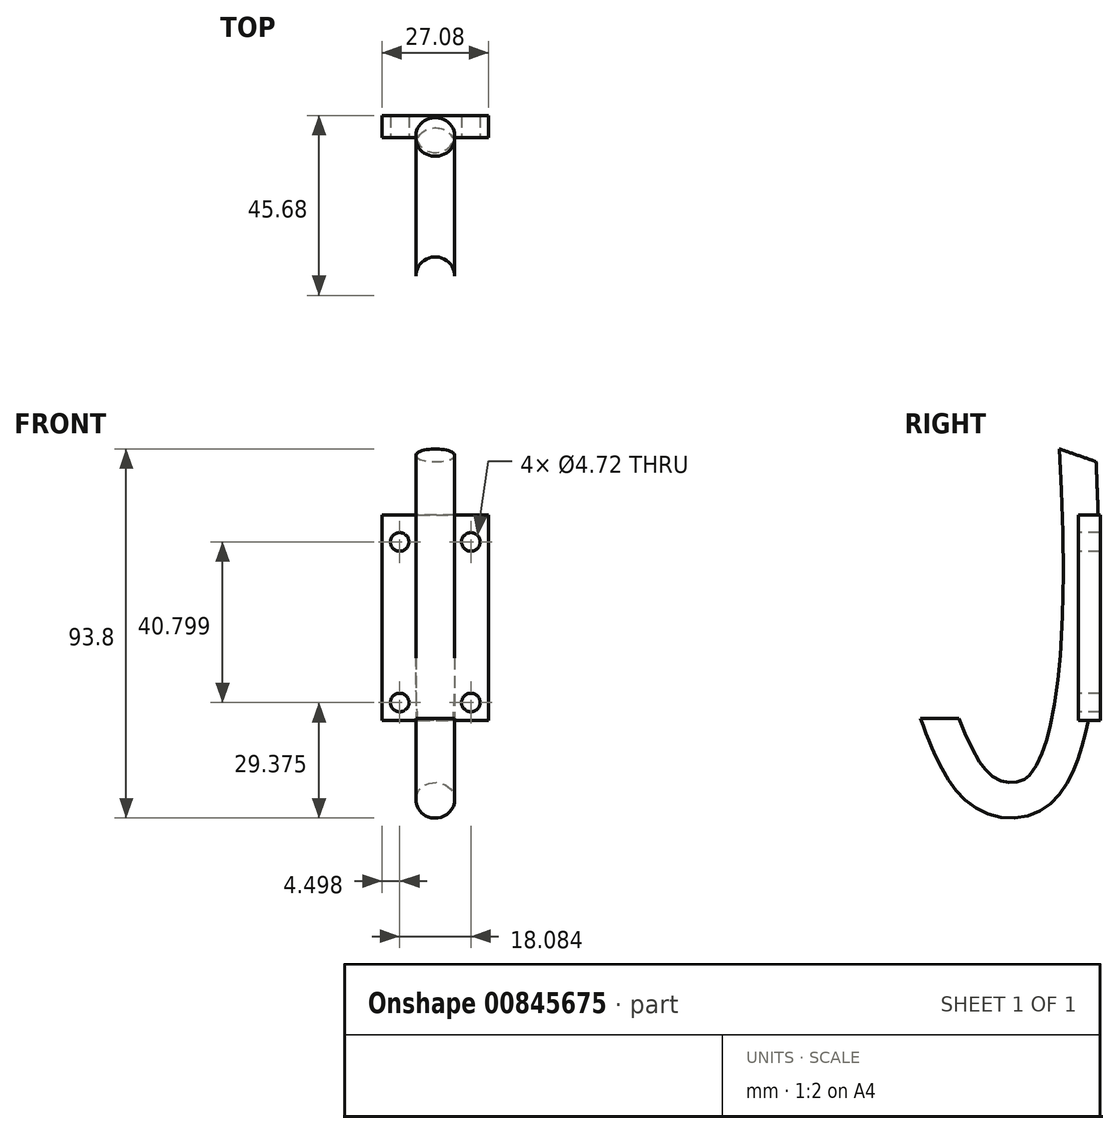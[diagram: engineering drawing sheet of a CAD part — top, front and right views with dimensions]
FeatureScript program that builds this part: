
annotation { "Feature Type Name" : "Feature", "Feature Type Description" : "" }
export const myFeature = defineFeature(function(context is Context, id is Id, definition is map)
    precondition{}
    {
        {
            var Q0;
            Q0=qCreatedBy(makeId("Right.planeOp"),FACE);
            var sketch = newSketch(context, id + "F0", { "sketchPlane" : qUnion([Q0])});
            skLineSegment(sketch, "E0", {"start": v(0, 15.71) * mm, "end": v(0, -33.2) * mm});
            skFitSpline(sketch, "E1", {"points": [v(0, 31.36) * mm, v(0, -21.22) * mm, v(-10.38, -53.96) * mm, v(-24.21, -53.96) * mm, v(-35.28, -35.51) * mm], "startDerivative": vector(6.73, -156.7) * mm, "endDerivative": vector(-40.88, 103.45) * mm});
            skSolve(sketch);
        }
        {
            var Q0;
            Q0=qCreatedBy(makeId("Top.planeOp"),FACE);
            cPlane(context, id + "F1", {"entities" : qUnion([Q0]), "cplaneType" : CPlaneType.OFFSET, "offset" : 36 * mm, "oppositeDirection" : true, "width" : 150 * mm, "height" : 150 * mm});
        }
        {
            var Q0;
            Q0=qCreatedBy(id+"F1.planeOp",FACE);
            var sketch = newSketch(context, id + "F2", { "sketchPlane" : qUnion([Q0])});
            skCircle(sketch, "E2", {"center": v(0, -34.98) * mm, "radius": 4.91 * mm});
            skSolve(sketch);
        }
        {
            var Q0;
            Q0=makeQuery(id+"F2.imprint","IMPRINT",FACE,{"disambiguationData":[TD([[makeQuery(id+"F2.imprint","IMPRINT",EDGE,{"derivedFrom":sQuery(id+"F2.wireOp",EDGE,"E2")}),1.0]])]});
            var Q1;
            Q1=sQuery(id+"F0.wireOp",EDGE,"E1");
            sweep(context, id + "F3", {"profiles" : qUnion([Q0]), "path" : qUnion([Q1])});
        }
        {
            var Q0;
            Q0=qCreatedBy(makeId("Front.planeOp"),FACE);
            var sketch = newSketch(context, id + "F4", { "sketchPlane" : qUnion([Q0])});
            skLineSegment(sketch, "E3", {"start": v(0, -35.99) * mm, "end": v(-13.54, -35.99) * mm});
            skLineSegment(sketch, "E4", {"start": v(-13.54, -35.99) * mm, "end": v(-13.54, 16.2) * mm});
            skLineSegment(sketch, "E5", {"start": v(0, 16.2) * mm, "end": v(-13.54, 16.2) * mm});
            skPoint(sketch, "E6.start.orphan", {"position": v(0, -10.21) * mm});
            skLineSegment(sketch, "E7.MirrorCS", {"start": v(13.54, -35.99) * mm, "end": v(13.54, 16.2) * mm});
            skLineSegment(sketch, "E8.MirrorCS", {"start": v(0, 16.2) * mm, "end": v(13.54, 16.2) * mm});
            skLineSegment(sketch, "E9.MirrorCS", {"start": v(0, -35.99) * mm, "end": v(13.54, -35.99) * mm});
            skSolve(sketch);
        }
        {
            var Q0;
            Q0 = qSketchRegion(id + "F4", true);
            extrude(context, id + "F5", {"entities" : qUnion([Q0]), "operationType" : NewBodyOperationType.ADD, "oppositeDirection" : true, "depth" : 5.6 * mm, "offsetDistance" : 25 * mm});
        }
        {
            var Q0;
            {var subQ0=sQuery(id+"F4.wireOp",EDGE,"E8.MirrorCS");var subQ1=sQuery(id+"F4.wireOp",EDGE,"E5");var subQ2=sQuery(id+"F4.wireOp",EDGE,"E9.MirrorCS");var subQ3=sQuery(id+"F4.wireOp",EDGE,"E3");var subQ4=sQuery(id+"F4.wireOp",EDGE,"E7.MirrorCS");Q0=makeQuery(id+"F5.boolean.opBoolean","SPLIT",FACE,{"disambiguationData":[TD([makeQuery(id+"F5.opExtrude","SWEPT_FACE",FACE,{"disambiguationData":[OSD([subQ4])]})])],"derivedFrom":makeQuery(id+"F5.opExtrude","CAP_FACE",FACE,{"disambiguationData":[OSD([subQ3,sQuery(id+"F4.wireOp",EDGE,"E4"),subQ1,subQ4,subQ0,subQ2])],"isStart":true})});}
            var sketch = newSketch(context, id + "F6", { "sketchPlane" : qUnion([Q0])});
            skCircle(sketch, "E10", {"center": v(-9.04, -31.41) * mm, "radius": 2.36 * mm});
            skCircle(sketch, "E11.MirrorC", {"center": v(9.04, -31.41) * mm, "radius": 2.36 * mm});
            skCircle(sketch, "E12", {"center": v(-9.04, 9.38) * mm, "radius": 2.36 * mm});
            skCircle(sketch, "E13.MirrorC", {"center": v(9.04, 9.38) * mm, "radius": 2.36 * mm});
            skSolve(sketch);
        }
        {
            var Q0;
            Q0 = qSketchRegion(id + "F6", true);
            extrude(context, id + "F7", {"entities" : qUnion([Q0]), "operationType" : NewBodyOperationType.REMOVE, "endBound" : BoundingType.THROUGH_ALL, "oppositeDirection" : true, "depth" : 25 * mm, "offsetDistance" : 25 * mm});
        }
    });
